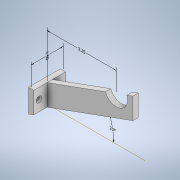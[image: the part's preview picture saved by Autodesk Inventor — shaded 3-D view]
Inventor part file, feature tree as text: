
AUTODESK INVENTOR PART (.ipt)
format: ipt  version: 2021.1 (Build 251245010, 245A)  size: 362,496 bytes
history: native  units: in
note: dims shown in document units (in); Inventor stores cm internally (conversion verified against a paired STEP export)
features: sketch x5, other x4, extrude x4, hole x1
ambient origin geometry x8: Origin, YZ Plane, XZ Plane, XY Plane, X Axis, Y Axis, Z Axis, Center Point
bodies: Solid2 (feature_tree)
feature tree (14):
  other  "Annotations"
  extrude  "Extrusion3"  Depth=0.25in
  extrude  "Extrusion4"  Depth=0.1374in
  sketch  "Sketch7"  dims[d26=1.075in d29=0.25in]
  extrude  "Extrusion5"  Depth=0.25in
  hole  "Hole3"  [1 undecoded]
  extrude  "Extrusion6"  TaperAngle=0.0deg  [1 undecoded]
  sketch  "Sketch5"  dims[d21=1.0in d22=0.25in]
  sketch  "Sketch6"  dims[d23=1.5in d24=0.0in d25=0.1374in]
  sketch  "Sketch8"  dims[d30=3.5in d31=0.25in]
  sketch  "Sketch9"  dims[d32=0.0in d33=0.0in d34=0.25in d35=0.25in d47=1.5in d48=0.0in d49=0.15in d50=0.75in d51=0.279in d52=0.25in d53=0.5635in d54=1.0in d55=0.8108in d62=0.05in d63=0.0in d56=0.2085in d57=0.331in d58=1.5in d59=2.3174in d60=0.1374in d61=3.25in]
  other  "Linear Dimension 1"
  other  "Angular Dimension 1"
  other  "Linear Dimension 2"
note: 2 required parameter values undecoded (feature->parameter linkage not recoverable at this tier; creation-order binding heuristic only, values carry confidence <= 0.55)
